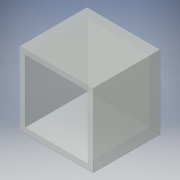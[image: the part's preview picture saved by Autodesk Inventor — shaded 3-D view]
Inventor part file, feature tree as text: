
AUTODESK INVENTOR PART (.ipt)
format: ipt  version: 2016 (Build 200138000, 138)  size: 103,936 bytes
history: native  units: mm
features: extrude x2, sketch x2
ambient origin geometry x8: Origin, YZ Plane, XZ Plane, XY Plane, X Axis, Y Axis, Z Axis, Center Point
bodies: Solid1 (feature_tree)
feature tree (4):
  extrude  "Extrusion1"  Depth=35.0mm
  extrude  "Extrusion2"  Depth=30.0mm
  sketch  "Sketch1"  dims[d0=35.0mm d1=35.0mm]
  sketch  "Sketch2"  dims[d2=30.0mm d3=30.0mm d4=30.0mm d5=0.0mm d6=2.0mm d7=0.0mm]
